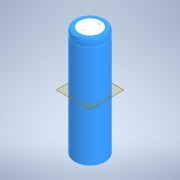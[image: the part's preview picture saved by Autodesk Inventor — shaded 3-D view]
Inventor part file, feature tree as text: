
AUTODESK INVENTOR PART (.ipt)
format: ipt  version: 2022 (Build 260153000, 153)  size: 722,944 bytes
history: native  units: mm
features: other x18, extrude x2, fillet x1
ambient origin geometry x8: Origin, YZ Plane, XZ Plane, XY Plane, X Axis, Y Axis, Z Axis, Center Point
bodies: Body1 (feature_tree), Body2 (feature_tree), Body3 (feature_tree), Body4 (feature_tree), Body5 (feature_tree), Body6 (feature_tree), Body7 (feature_tree), Body8 (feature_tree), Body9 (feature_tree), Body10 (feature_tree)
feature tree (21):
  other  "Твердое тело1"
  other  "РабПлоскость1"
  other  "Твердое тело2"
  other  "Твердое тело3"
  other  "Твердое тело4"
  other  "Твердое тело5"
  other  "Твердое тело6"
  other  "Твердое тело7"
  other  "Твердое тело8"
  other  "Твердое тело9"
  other  "Твердое тело10"
  other  "Kan"
  other  "GasketCut"
  other  "TopGasket"
  other  "(+) Spacer"
  other  "(+) TopCut"
  other  "Ring"
  other  "Seal"
  fillet  "Fillet1"  [1 undecoded]
  extrude  "Extrude3"  [1 undecoded]
  extrude  "Extrude4"  [1 undecoded]
note: 3 required parameter values undecoded (feature->parameter linkage not recoverable at this tier; creation-order binding heuristic only, values carry confidence <= 0.55)
